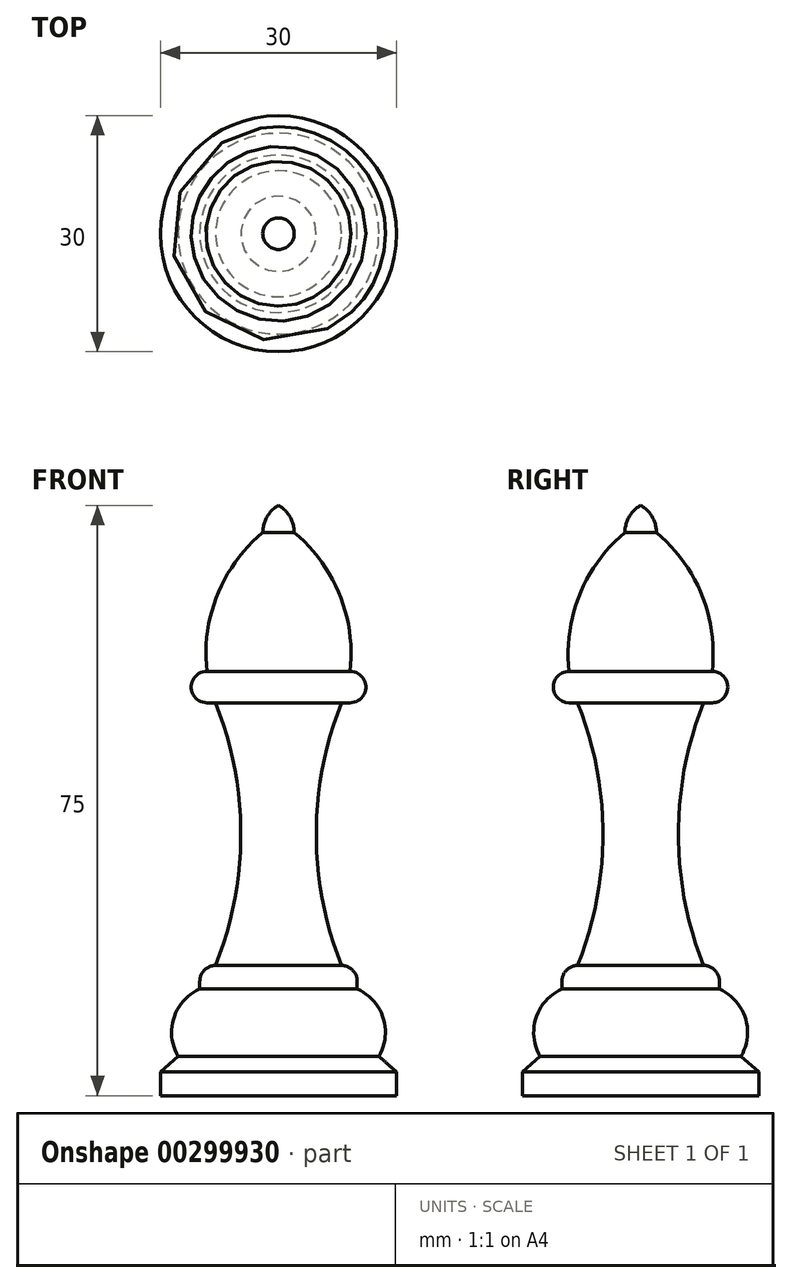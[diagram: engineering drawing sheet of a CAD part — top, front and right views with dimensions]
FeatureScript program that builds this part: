
annotation { "Feature Type Name" : "Feature", "Feature Type Description" : "" }
export const myFeature = defineFeature(function(context is Context, id is Id, definition is map)
    precondition{}
    {
        {
            var Q0;
            Q0=qCreatedBy(makeId("Front.planeOp"),FACE);
            var sketch = newSketch(context, id + "F0", { "sketchPlane" : qUnion([Q0])});
            skArc(sketch, "E0", {"start": v(9.09, -25.1) * mm, "mid": v(11.09, -23.1) * mm, "end": v(9.09, -21.1) * mm});
            skLineSegment(sketch, "E1", {"start": v(9.09, -25.1) * mm, "end": v(8, -25.1) * mm});
            skArc(sketch, "E2", {"start": v(10, -60.46) * mm, "mid": v(9.41, -59.05) * mm, "end": v(8, -58.46) * mm});
            skLineSegment(sketch, "E3", {"start": v(10, -60.46) * mm, "end": v(10, -61.46) * mm});
            skArc(sketch, "E4", {"start": v(12.75, -70) * mm, "mid": v(13.3, -65.11) * mm, "end": v(10, -61.46) * mm});
            skLineSegment(sketch, "E5", {"start": v(12.75, -70) * mm, "end": v(15, -72) * mm});
            skLineSegment(sketch, "E6", {"start": v(15, -72) * mm, "end": v(15, -72) * mm});
            skLineSegment(sketch, "E7", {"start": v(15, -75) * mm, "end": v(0, -75) * mm});
            skLineSegment(sketch, "E8", {"start": v(0, -75) * mm, "end": v(0, -75) * mm});
            skLineSegment(sketch, "E9", {"start": v(0, 0) * mm, "end": v(0, -75) * mm});
            skArc(sketch, "E10", {"start": v(2, -3.46) * mm, "mid": v(1.46, -1.46) * mm, "end": v(0, 0) * mm});
            skArc(sketch, "E11", {"start": v(9.09, -21.1) * mm, "mid": v(7.77, -11.38) * mm, "end": v(2, -3.46) * mm});
            skLineSegment(sketch, "E12", {"start": v(15, -75) * mm, "end": v(15, -72) * mm});
            skArc(sketch, "E13", {"start": v(8, -25.1) * mm, "mid": v(4.8, -41.78) * mm, "end": v(8, -58.46) * mm});
            skSolve(sketch);
        }
        {
            var Q0;
            Q0=makeQuery(id+"F0.imprint","IMPRINT",FACE,{"disambiguationData":[TD([[makeQuery(id+"F0.imprint","IMPRINT",EDGE,{"derivedFrom":sQuery(id+"F0.wireOp",EDGE,"E0")}),1.0]])]});
            var Q1;
            Q1=sQuery(id+"F0.wireOp",EDGE,"E9");
            revolve(context, id + "F1", {"entities" : qUnion([Q0]), "axis" : qUnion([Q1]), "revolveType" : RevolveType.FULL});
        }
    });
